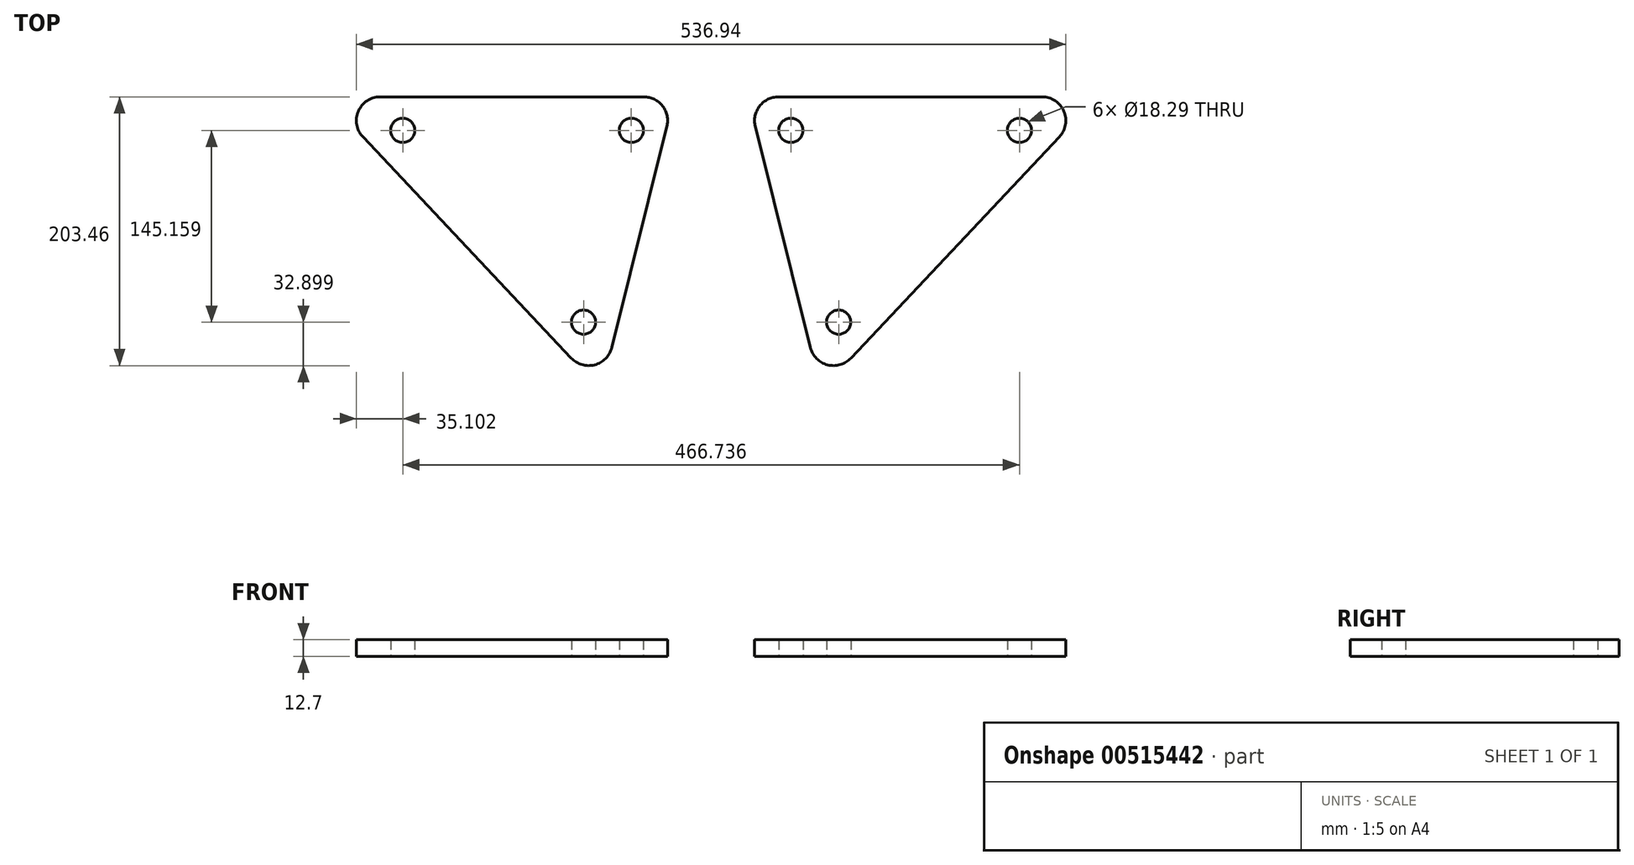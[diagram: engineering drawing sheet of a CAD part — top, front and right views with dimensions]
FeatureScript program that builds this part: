
annotation { "Feature Type Name" : "Feature", "Feature Type Description" : "" }
export const myFeature = defineFeature(function(context is Context, id is Id, definition is map)
    precondition{}
    {
        {
            var Q0;
            Q0=qCreatedBy(makeId("Top.planeOp"),FACE);
            var sketch = newSketch(context, id + "F0", { "sketchPlane" : qUnion([Q0])});
            skLineSegment(sketch, "E0", {"start": v(292.21, 105.6) * mm, "end": v(27.85, 105.6) * mm});
            skLineSegment(sketch, "E1", {"start": v(27.85, 105.6) * mm, "end": v(83.16, -116.2) * mm});
            skLineSegment(sketch, "E2", {"start": v(83.16, -116.2) * mm, "end": v(292.21, 105.6) * mm});
            skCircle(sketch, "E3", {"center": v(96.56, -64.95) * mm, "radius": 9.14 * mm});
            skLineSegment(sketch, "E4", {"start": v(71.91, -71.1) * mm, "end": v(96.56, -64.95) * mm, "construction": true});
            skLineSegment(sketch, "E5", {"start": v(96.56, -64.95) * mm, "end": v(115.04, -82.37) * mm, "construction": true});
            skCircle(sketch, "E6", {"center": v(60.36, 80.2) * mm, "radius": 9.14 * mm});
            skCircle(sketch, "E7", {"center": v(233.37, 80.2) * mm, "radius": 9.14 * mm});
            skLineSegment(sketch, "E8", {"start": v(60.36, 80.2) * mm, "end": v(35.72, 74.06) * mm, "construction": true});
            skLineSegment(sketch, "E9", {"start": v(60.36, 105.6) * mm, "end": v(60.36, 80.2) * mm, "construction": true});
            skLineSegment(sketch, "E10", {"start": v(233.37, 80.2) * mm, "end": v(233.37, 105.6) * mm, "construction": true});
            skLineSegment(sketch, "E11", {"start": v(233.37, 80.2) * mm, "end": v(251.85, 62.79) * mm, "construction": true});
            skSolve(sketch);
        }
        {
            var Q0;
            Q0=makeQuery(id+"F0.imprint","IMPRINT",FACE,{"disambiguationData":[TD([[makeQuery(id+"F0.imprint","IMPRINT",EDGE,{"derivedFrom":sQuery(id+"F0.wireOp",EDGE,"E0")}),1.0]])]});
            extrude(context, id + "F1", {"entities" : qUnion([Q0]), "depth" : 12.7 * mm, "offsetDistance" : 25.4 * mm});
        }
        {
            var Q0;
            Q0=makeQuery(id+"F1.opExtrude","SWEPT_EDGE",EDGE,{"disambiguationData":[OSD([sQuery(id+"F0.wireOp",EDGE,"E1"),sQuery(id+"F0.wireOp",EDGE,"E2")])]});
            var Q1;
            Q1=makeQuery(id+"F1.opExtrude","SWEPT_EDGE",EDGE,{"disambiguationData":[OSD([sQuery(id+"F0.wireOp",EDGE,"E0"),sQuery(id+"F0.wireOp",EDGE,"E2")])]});
            var Q2;
            Q2=makeQuery(id+"F1.opExtrude","SWEPT_EDGE",EDGE,{"disambiguationData":[OSD([sQuery(id+"F0.wireOp",EDGE,"E0"),sQuery(id+"F0.wireOp",EDGE,"E1")])]});
            fillet(context, id + "F2", {"entities" : qUnion([Q0, Q1, Q2]), "radius" : 18.03 * mm, "tangentPropagation" : true, "allowEdgeOverflow" : false});
        }
        {
            var Q0;
            Q0=makeQuery(id+"F1.opExtrude","SWEPT_BODY",BODY,{"disambiguationData":[OSD([sQuery(id+"F0.wireOp",EDGE,"E0"),sQuery(id+"F0.wireOp",EDGE,"E1"),sQuery(id+"F0.wireOp",EDGE,"E2"),sQuery(id+"F0.wireOp",EDGE,"E3"),sQuery(id+"F0.wireOp",EDGE,"E6"),sQuery(id+"F0.wireOp",EDGE,"E7")])]});
            var Q1;
            Q1=qCreatedBy(makeId("Right.planeOp"),FACE);
            mirror(context, id + "F3", {"entities" : qUnion([Q0]), "mirrorPlane" : qUnion([Q1])});
        }
    });
